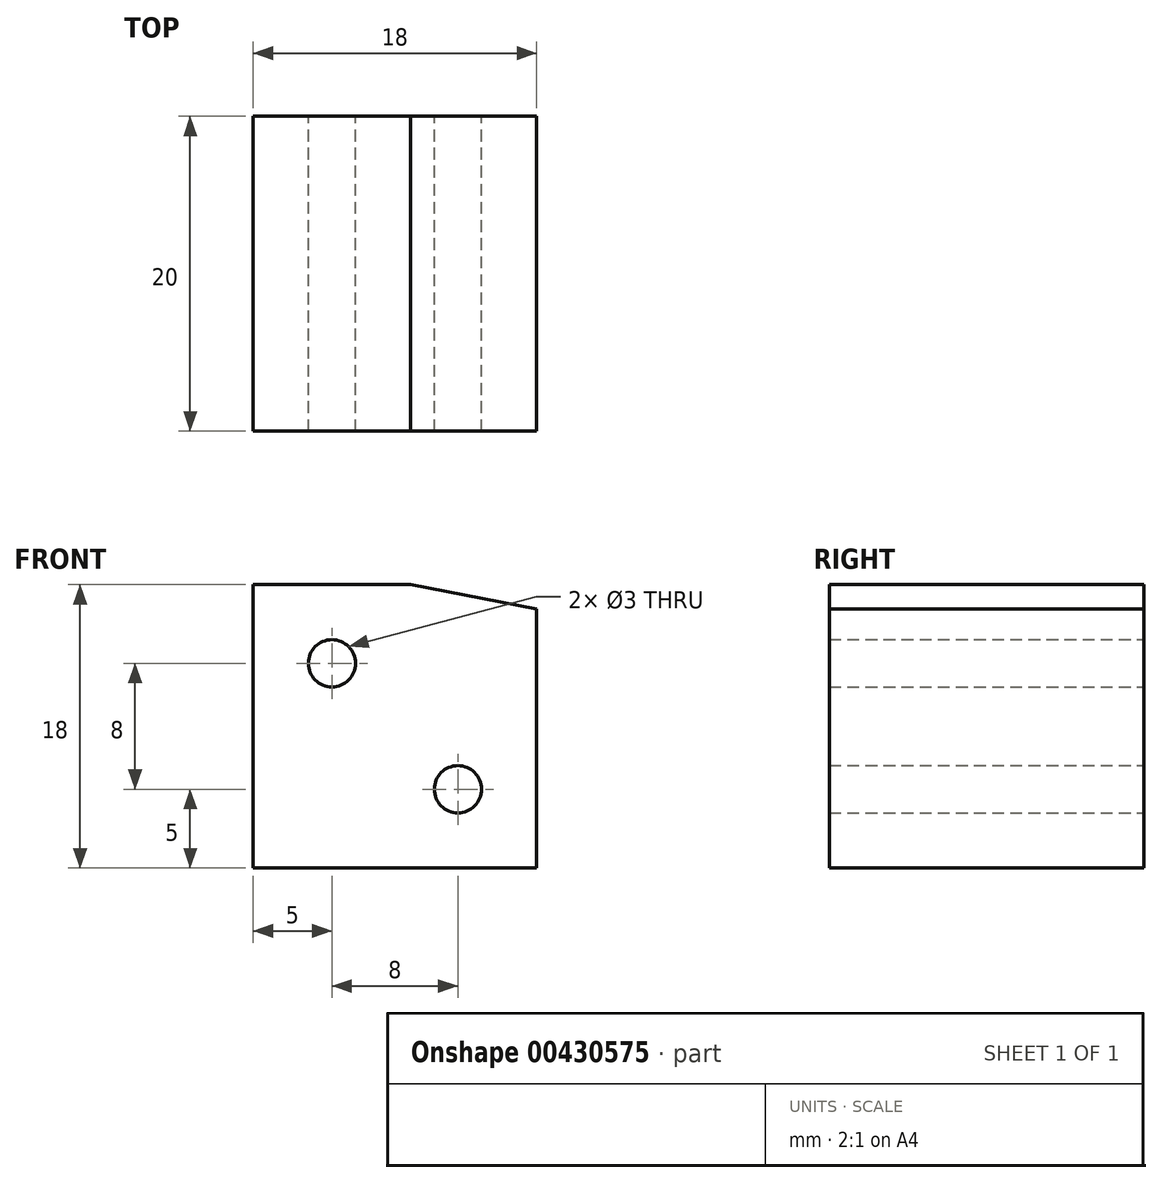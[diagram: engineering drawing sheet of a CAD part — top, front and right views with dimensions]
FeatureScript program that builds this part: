
annotation { "Feature Type Name" : "Feature", "Feature Type Description" : "" }
export const myFeature = defineFeature(function(context is Context, id is Id, definition is map)
    precondition{}
    {
        {
            var Q0;
            Q0=qCreatedBy(makeId("Front.planeOp"),FACE);
            var sketch = newSketch(context, id + "F0", { "sketchPlane" : qUnion([Q0])});
            skLineSegment(sketch, "E0", {"start": v(-5, 6) * mm, "end": v(-5, 24) * mm});
            skLineSegment(sketch, "E1", {"start": v(-5, 24) * mm, "end": v(5, 24) * mm});
            skLineSegment(sketch, "E2", {"start": v(5, 24) * mm, "end": v(13, 22.44) * mm});
            skLineSegment(sketch, "E3", {"start": v(46, 16) * mm, "end": v(56, 16) * mm, "construction": true});
            skLineSegment(sketch, "E4", {"start": v(56, 16) * mm, "end": v(56, 6) * mm, "construction": true});
            skLineSegment(sketch, "E5", {"start": v(56, 6) * mm, "end": v(13, 6) * mm, "construction": true});
            skCircle(sketch, "E6", {"center": v(0, 19) * mm, "radius": 1.5 * mm});
            skCircle(sketch, "E7", {"center": v(8, 11) * mm, "radius": 1.5 * mm});
            skLineSegment(sketch, "E8", {"start": v(13, 22.44) * mm, "end": v(13, 6) * mm});
            skLineSegment(sketch, "E9", {"start": v(13, 22.44) * mm, "end": v(46, 16) * mm, "construction": true});
            skLineSegment(sketch, "E10", {"start": v(13, 6) * mm, "end": v(-5, 6) * mm});
            skSolve(sketch);
        }
        {
            var Q0;
            Q0=makeQuery(id+"F0.imprint","IMPRINT",FACE,{"disambiguationData":[TD([[makeQuery(id+"F0.imprint","IMPRINT",EDGE,{"derivedFrom":sQuery(id+"F0.wireOp",EDGE,"645f92d7-41c5-44ff-aa7f-0d42a2d06cf7")}),1.0]])]});
            var Q1;
            Q1=makeQuery(id+"F0.imprint","IMPRINT",FACE,{"disambiguationData":[TD([[makeQuery(id+"F0.imprint","IMPRINT",EDGE,{"derivedFrom":sQuery(id+"F0.wireOp",EDGE,"E0")}),-1.0]])]});
            extrude(context, id + "F1", {"entities" : qUnion([Q0, Q1]), "endBound" : BoundingType.SYMMETRIC, "depth" : 20 * mm, "offsetDistance" : 25 * mm});
        }
    });
